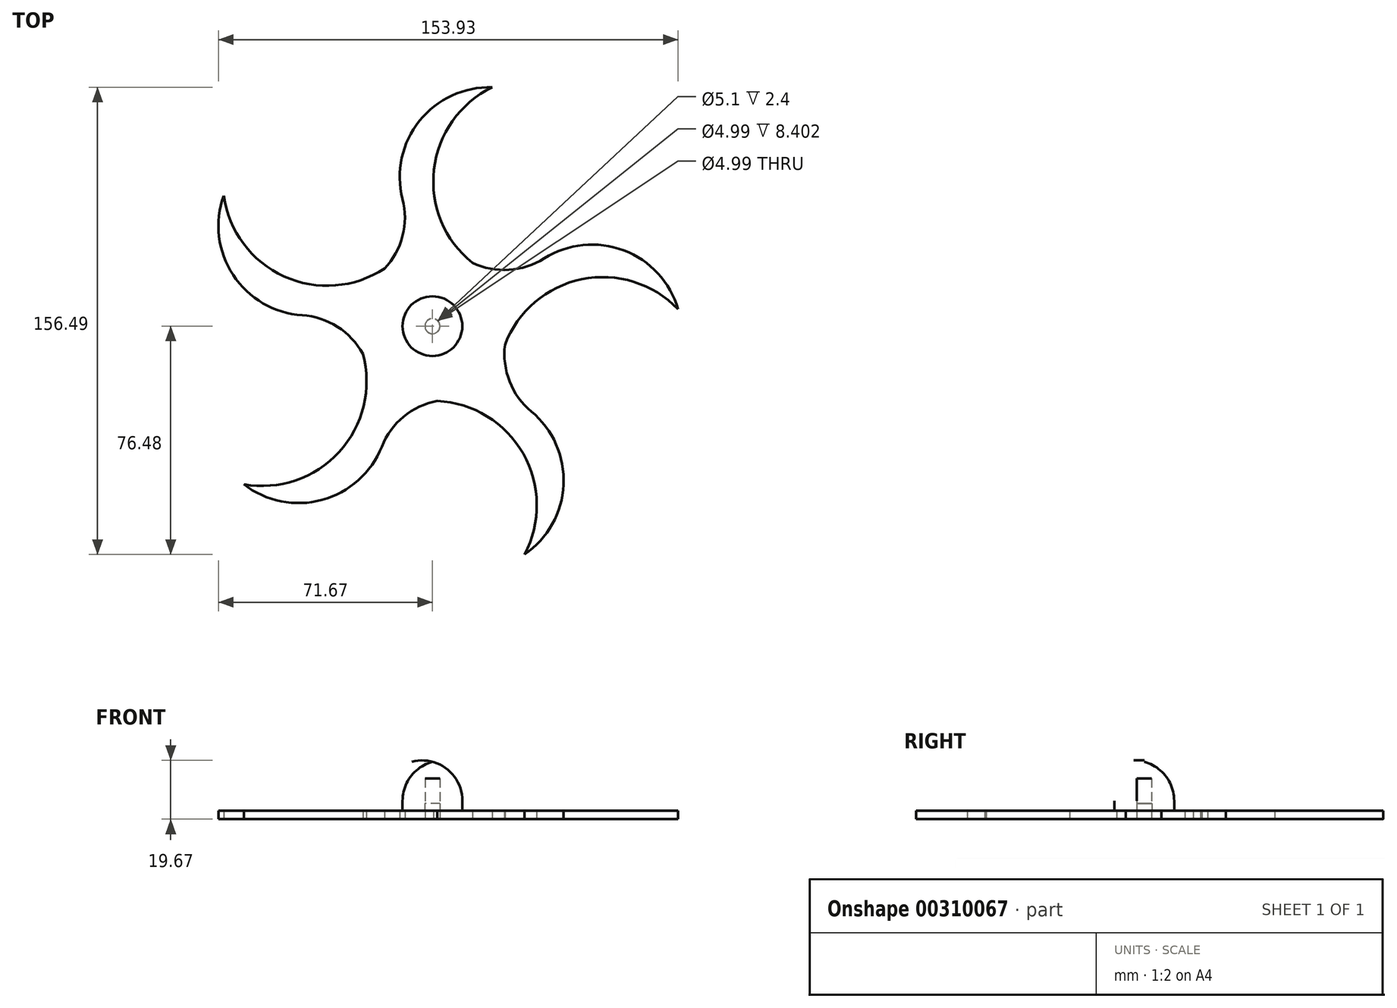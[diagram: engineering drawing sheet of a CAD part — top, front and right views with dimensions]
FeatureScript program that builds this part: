
annotation { "Feature Type Name" : "Feature", "Feature Type Description" : "" }
export const myFeature = defineFeature(function(context is Context, id is Id, definition is map)
    precondition{}
    {
        {
            var Q0;
            Q0=qCreatedBy(makeId("Top.planeOp"),FACE);
            var sketch = newSketch(context, id + "F0", { "sketchPlane" : qUnion([Q0])});
            skCircle(sketch, "E0", {"center": v(0, 0) * mm, "radius": 2.5 * mm});
            skCircle(sketch, "E1", {"center": v(0, 0) * mm, "radius": 25 * mm});
            skArc(sketch, "E2", {"start": v(20, 80) * mm, "mid": v(0.43, 51.6) * mm, "end": v(14.7, 20.22) * mm});
            skArc(sketch, "E3", {"start": v(20, 80) * mm, "mid": v(-9.56, 58.97) * mm, "end": v(2.74, 24.85) * mm});
            skArc(sketch, "E4", {"start": v(-17.11, 18.22) * mm, "mid": v(-10.23, 29.45) * mm, "end": v(-10, 42.61) * mm});
            skArc(sketch, "E5.1.0", {"start": v(-22.62, -10.64) * mm, "mid": v(-31.17, -0.63) * mm, "end": v(-43.62, 3.66) * mm});
            skArc(sketch, "E5.1.1", {"start": v(-69.9, 43.74) * mm, "mid": v(-59.04, 9.13) * mm, "end": v(-22.79, 10.29) * mm});
            skArc(sketch, "E5.1.2", {"start": v(-69.9, 43.74) * mm, "mid": v(-48.95, 16.36) * mm, "end": v(-14.68, 20.23) * mm});
            skArc(sketch, "E5.2.0", {"start": v(3.13, -24.8) * mm, "mid": v(-9.04, -29.84) * mm, "end": v(-16.96, -40.35) * mm});
            skArc(sketch, "E5.2.1", {"start": v(-63.2, -52.97) * mm, "mid": v(-26.93, -53.33) * mm, "end": v(-16.82, -18.5) * mm});
            skArc(sketch, "E5.2.2", {"start": v(-63.2, -52.97) * mm, "mid": v(-30.68, -41.5) * mm, "end": v(-23.78, -7.71) * mm});
            skArc(sketch, "E6.4.3.0", {"start": v(30.84, -76.48) * mm, "mid": v(42.4, -42.1) * mm, "end": v(12.39, -21.71) * mm});
            skArc(sketch, "E6.7.3.0", {"start": v(24.56, -4.68) * mm, "mid": v(25.58, -17.81) * mm, "end": v(33.14, -28.6) * mm});
            skArc(sketch, "E6.8.3.0", {"start": v(30.84, -76.48) * mm, "mid": v(29.98, -42) * mm, "end": v(-0.02, -25) * mm});
            skArc(sketch, "E7.4.4.0", {"start": v(82.26, 5.7) * mm, "mid": v(53.13, 27.31) * mm, "end": v(24.48, 5.07) * mm});
            skArc(sketch, "E7.7.4.0", {"start": v(12.04, 21.9) * mm, "mid": v(24.85, 18.83) * mm, "end": v(37.44, 22.68) * mm});
            skArc(sketch, "E7.8.4.0", {"start": v(82.26, 5.7) * mm, "mid": v(49.21, 15.54) * mm, "end": v(23.77, -7.74) * mm});
            skSolve(sketch);
        }
        {
            var Q0;
            {var subQ4=sQuery(id+"F0.wireOp",EDGE,"E1");var subQ6=sQuery(id+"F0.wireOp",EDGE,"E4");var subQ7=makeQuery(id+"F0.imprint","INTERSECT",VERTEX,{"derivedFrom":[subQ4,subQ6]});Q0=makeQuery(id+"F0.imprint","IMPRINT",FACE,{"disambiguationData":[TD([[makeQuery(id+"F0.imprint","IMPRINT",EDGE,{"disambiguationData":[TD([[subQ7,-1.0]])],"derivedFrom":subQ4}),-1.0]])]});}
            var Q1;
            {var subQ0=sQuery(id+"F0.wireOp",EDGE,"E5.1.1");var subQ1=sQuery(id+"F0.wireOp",EDGE,"E1");var subQ2=makeQuery(id+"F0.imprint","INTERSECT",VERTEX,{"derivedFrom":[subQ1,subQ0]});Q1=makeQuery(id+"F0.imprint","IMPRINT",FACE,{"disambiguationData":[TD([[makeQuery(id+"F0.imprint","IMPRINT",EDGE,{"disambiguationData":[TD([[subQ2,-1.0]])],"derivedFrom":subQ1}),-1.0]])]});}
            var Q2;
            {var subQ0=sQuery(id+"F0.wireOp",EDGE,"E3");var subQ1=sQuery(id+"F0.wireOp",EDGE,"E1");var subQ2=makeQuery(id+"F0.imprint","INTERSECT",VERTEX,{"derivedFrom":[subQ1,subQ0]});Q2=makeQuery(id+"F0.imprint","IMPRINT",FACE,{"disambiguationData":[TD([[makeQuery(id+"F0.imprint","IMPRINT",EDGE,{"disambiguationData":[TD([[subQ2,-1.0]])],"derivedFrom":subQ1}),-1.0]])]});}
            var Q3;
            {var subQ0=sQuery(id+"F0.wireOp",EDGE,"E4");var subQ1=sQuery(id+"F0.wireOp",EDGE,"E1");var subQ2=makeQuery(id+"F0.imprint","INTERSECT",VERTEX,{"derivedFrom":[subQ1,subQ0]});Q3=makeQuery(id+"F0.imprint","IMPRINT",FACE,{"disambiguationData":[TD([[makeQuery(id+"F0.imprint","IMPRINT",EDGE,{"disambiguationData":[TD([[subQ2,1.0]])],"derivedFrom":subQ1}),-1.0]])]});}
            var Q4;
            Q4=makeQuery(id+"F0.imprint","IMPRINT",FACE,{"disambiguationData":[TD([[makeQuery(id+"F0.imprint","IMPRINT",EDGE,{"derivedFrom":sQuery(id+"F0.wireOp",EDGE,"E0")}),-1.0]])]});
            var Q5;
            {var subQ0=sQuery(id+"F0.wireOp",EDGE,"E3");var subQ1=sQuery(id+"F0.wireOp",EDGE,"E1");var subQ2=makeQuery(id+"F0.imprint","INTERSECT",VERTEX,{"derivedFrom":[subQ1,subQ0]});Q5=makeQuery(id+"F0.imprint","IMPRINT",FACE,{"disambiguationData":[TD([[makeQuery(id+"F0.imprint","IMPRINT",EDGE,{"disambiguationData":[TD([[subQ2,1.0]])],"derivedFrom":subQ1}),-1.0]])]});}
            var Q6;
            {var subQ0=sQuery(id+"F0.wireOp",EDGE,"E2");var subQ1=sQuery(id+"F0.wireOp",EDGE,"E1");var subQ2=makeQuery(id+"F0.imprint","INTERSECT",VERTEX,{"derivedFrom":[subQ1,subQ0]});Q6=makeQuery(id+"F0.imprint","IMPRINT",FACE,{"disambiguationData":[TD([[makeQuery(id+"F0.imprint","IMPRINT",EDGE,{"disambiguationData":[TD([[subQ2,1.0]])],"derivedFrom":subQ1}),-1.0]])]});}
            var Q7;
            {var subQ1=sQuery(id+"F0.wireOp",EDGE,"E1");var subQ4=sQuery(id+"F0.wireOp",EDGE,"E6.7.3.0");var subQ5=makeQuery(id+"F0.imprint","INTERSECT",VERTEX,{"derivedFrom":[subQ1,subQ4]});Q7=makeQuery(id+"F0.imprint","IMPRINT",FACE,{"disambiguationData":[TD([[makeQuery(id+"F0.imprint","IMPRINT",EDGE,{"disambiguationData":[TD([[subQ5,-1.0]])],"derivedFrom":subQ1}),-1.0]])]});}
            var Q8;
            {var subQ0=sQuery(id+"F0.wireOp",EDGE,"E6.4.3.0");var subQ1=sQuery(id+"F0.wireOp",EDGE,"E1");var subQ2=makeQuery(id+"F0.imprint","INTERSECT",VERTEX,{"derivedFrom":[subQ1,subQ0]});Q8=makeQuery(id+"F0.imprint","IMPRINT",FACE,{"disambiguationData":[TD([[makeQuery(id+"F0.imprint","IMPRINT",EDGE,{"disambiguationData":[TD([[subQ2,-1.0]])],"derivedFrom":subQ1}),-1.0]])]});}
            var Q9;
            {var subQ1=sQuery(id+"F0.wireOp",EDGE,"E1");var subQ6=sQuery(id+"F0.wireOp",EDGE,"E5.2.0");var subQ7=makeQuery(id+"F0.imprint","INTERSECT",VERTEX,{"derivedFrom":[subQ1,subQ6]});Q9=makeQuery(id+"F0.imprint","IMPRINT",FACE,{"disambiguationData":[TD([[makeQuery(id+"F0.imprint","IMPRINT",EDGE,{"disambiguationData":[TD([[subQ7,-1.0]])],"derivedFrom":subQ1}),-1.0]])]});}
            var Q10;
            {var subQ0=sQuery(id+"F0.wireOp",EDGE,"E5.2.1");var subQ1=sQuery(id+"F0.wireOp",EDGE,"E1");var subQ2=makeQuery(id+"F0.imprint","INTERSECT",VERTEX,{"derivedFrom":[subQ1,subQ0]});Q10=makeQuery(id+"F0.imprint","IMPRINT",FACE,{"disambiguationData":[TD([[makeQuery(id+"F0.imprint","IMPRINT",EDGE,{"disambiguationData":[TD([[subQ2,-1.0]])],"derivedFrom":subQ1}),-1.0]])]});}
            var Q11;
            {var subQ2=sQuery(id+"F0.wireOp",EDGE,"E1");var subQ4=sQuery(id+"F0.wireOp",EDGE,"E5.1.0");var subQ5=makeQuery(id+"F0.imprint","INTERSECT",VERTEX,{"derivedFrom":[subQ2,subQ4]});Q11=makeQuery(id+"F0.imprint","IMPRINT",FACE,{"disambiguationData":[TD([[makeQuery(id+"F0.imprint","IMPRINT",EDGE,{"disambiguationData":[TD([[subQ5,-1.0]])],"derivedFrom":subQ2}),-1.0]])]});}
            var Q12;
            {var subQ0=sQuery(id+"F0.wireOp",EDGE,"E5.1.0");var subQ1=sQuery(id+"F0.wireOp",EDGE,"E1");var subQ2=makeQuery(id+"F0.imprint","INTERSECT",VERTEX,{"derivedFrom":[subQ1,subQ0]});Q12=makeQuery(id+"F0.imprint","IMPRINT",FACE,{"disambiguationData":[TD([[makeQuery(id+"F0.imprint","IMPRINT",EDGE,{"disambiguationData":[TD([[subQ2,1.0]])],"derivedFrom":subQ1}),-1.0]])]});}
            var Q13;
            {var subQ0=sQuery(id+"F0.wireOp",EDGE,"E5.2.0");var subQ1=sQuery(id+"F0.wireOp",EDGE,"E1");var subQ2=makeQuery(id+"F0.imprint","INTERSECT",VERTEX,{"derivedFrom":[subQ1,subQ0]});Q13=makeQuery(id+"F0.imprint","IMPRINT",FACE,{"disambiguationData":[TD([[makeQuery(id+"F0.imprint","IMPRINT",EDGE,{"disambiguationData":[TD([[subQ2,1.0]])],"derivedFrom":subQ1}),-1.0]])]});}
            var Q14;
            {var subQ0=sQuery(id+"F0.wireOp",EDGE,"E6.7.3.0");var subQ1=sQuery(id+"F0.wireOp",EDGE,"E1");var subQ2=makeQuery(id+"F0.imprint","INTERSECT",VERTEX,{"derivedFrom":[subQ1,subQ0]});Q14=makeQuery(id+"F0.imprint","IMPRINT",FACE,{"disambiguationData":[TD([[makeQuery(id+"F0.imprint","IMPRINT",EDGE,{"disambiguationData":[TD([[subQ2,1.0]])],"derivedFrom":subQ1}),-1.0]])]});}
            var Q15;
            {var subQ0=sQuery(id+"F0.wireOp",EDGE,"E2");var subQ1=sQuery(id+"F0.wireOp",EDGE,"E1");var subQ2=makeQuery(id+"F0.imprint","INTERSECT",VERTEX,{"derivedFrom":[subQ1,subQ0]});Q15=makeQuery(id+"F0.imprint","IMPRINT",FACE,{"disambiguationData":[TD([[makeQuery(id+"F0.imprint","IMPRINT",EDGE,{"disambiguationData":[TD([[subQ2,-1.0]])],"derivedFrom":subQ1}),-1.0]])]});}
            extrude(context, id + "F1", {"entities" : qUnion([Q0, Q1, Q2, Q3, Q4, Q5, Q6, Q7, Q8, Q9, Q10, Q11, Q12, Q13, Q14, Q15]), "depth" : 2.8 * mm});
        }
        {
            var Q0;
            Q0=makeQuery(id+"F1.opExtrude","CAP_FACE",FACE,{"disambiguationData":[OSD([sQuery(id+"F0.wireOp",EDGE,"E0"),sQuery(id+"F0.wireOp",EDGE,"E2"),sQuery(id+"F0.wireOp",EDGE,"E3"),sQuery(id+"F0.wireOp",EDGE,"E4"),sQuery(id+"F0.wireOp",EDGE,"E5.1.0"),sQuery(id+"F0.wireOp",EDGE,"E5.1.1"),sQuery(id+"F0.wireOp",EDGE,"E5.1.2"),sQuery(id+"F0.wireOp",EDGE,"E5.2.0"),sQuery(id+"F0.wireOp",EDGE,"E5.2.1"),sQuery(id+"F0.wireOp",EDGE,"E5.2.2"),sQuery(id+"F0.wireOp",EDGE,"E6.4.3.0"),sQuery(id+"F0.wireOp",EDGE,"E6.7.3.0"),sQuery(id+"F0.wireOp",EDGE,"E6.8.3.0"),sQuery(id+"F0.wireOp",EDGE,"E7.4.4.0"),sQuery(id+"F0.wireOp",EDGE,"E7.7.4.0"),sQuery(id+"F0.wireOp",EDGE,"E7.8.4.0")])],"isStart":false});
            var sketch = newSketch(context, id + "F2", { "sketchPlane" : qUnion([Q0])});
            skCircle(sketch, "E8.0", {"center": v(0, 0) * mm, "radius": 2.5 * mm});
            skCircle(sketch, "E9", {"center": v(0, 0) * mm, "radius": 10 * mm});
            skLineSegment(sketch, "E10", {"start": v(-10, 0) * mm, "end": v(-2.5, 0) * mm});
            skLineSegment(sketch, "E11", {"start": v(-2.5, 0) * mm, "end": v(2.5, 0) * mm});
            skLineSegment(sketch, "E12", {"start": v(2.5, 0) * mm, "end": v(10, 0) * mm});
            skCircle(sketch, "E13", {"center": v(0, 0) * mm, "radius": 2.55 * mm});
            skSolve(sketch);
        }
        {
            var Q0;
            {var subQ0=sQuery(id+"F2.wireOp",EDGE,"E10");var subQ1=sQuery(id+"F2.wireOp",EDGE,"E9");var subQ2=makeQuery(id+"F2.imprint","INTERSECT",VERTEX,{"derivedFrom":[subQ1,subQ0]});Q0=makeQuery(id+"F2.imprint","IMPRINT",FACE,{"disambiguationData":[TD([[makeQuery(id+"F2.imprint","IMPRINT",EDGE,{"disambiguationData":[TD([[subQ2,-1.0]])],"derivedFrom":subQ1}),1.0]])]});}
            var Q1;
            {var subQ0=sQuery(id+"F2.wireOp",EDGE,"E10");var subQ1=sQuery(id+"F2.wireOp",EDGE,"E9");var subQ2=makeQuery(id+"F2.imprint","INTERSECT",VERTEX,{"derivedFrom":[subQ1,subQ0]});Q1=makeQuery(id+"F2.imprint","IMPRINT",FACE,{"disambiguationData":[TD([[makeQuery(id+"F2.imprint","IMPRINT",EDGE,{"disambiguationData":[TD([[subQ2,1.0]])],"derivedFrom":subQ1}),1.0]])]});}
            extrude(context, id + "F3", {"entities" : qUnion([Q0, Q1]), "depth" : 2.4 * mm});
        }
        {
            var Q0;
            Q0=makeQuery(id+"F3.opExtrude","CAP_FACE",FACE,{"disambiguationData":[OSD([sQuery(id+"F2.wireOp",EDGE,"E8.0"),sQuery(id+"F2.wireOp",EDGE,"E9")])],"isStart":false});
            var sketch = newSketch(context, id + "F4", { "sketchPlane" : qUnion([Q0])});
            skLineSegment(sketch, "E14.0", {"start": v(-10, 0) * mm, "end": v(-2.5, 0) * mm});
            skLineSegment(sketch, "E15.0", {"start": v(2.5, 0) * mm, "end": v(10, 0) * mm});
            skCircle(sketch, "E16.0", {"center": v(0, 0) * mm, "radius": 10 * mm});
            skCircle(sketch, "E17.0", {"center": v(0, 0) * mm, "radius": 2.5 * mm});
            skSolve(sketch);
        }
        {
            var Q0;
            {var subQ0=sQuery(id+"F4.wireOp",EDGE,"E14.0");Q0=makeQuery(id+"F4.imprint","IMPRINT",FACE,{"disambiguationData":[TD([[makeQuery(id+"F4.imprint","IMPRINT",EDGE,{"derivedFrom":subQ0}),1.0]])]});}
            extrude(context, id + "F5", {"entities" : qUnion([Q0]), "depth" : 1 * mm});
        }
        {
            var Q0;
            Q0=makeQuery(id+"F5.opExtrude","SWEPT_FACE",FACE,{"disambiguationData":[OSD([sQuery(id+"F4.wireOp",EDGE,"E14.0")])]});
            var sketch = newSketch(context, id + "F6", { "sketchPlane" : qUnion([Q0])});
            skLineSegment(sketch, "E18.0", {"start": v(-10, 5.2) * mm, "end": v(10, 5.2) * mm});
            skLineSegment(sketch, "E19.0", {"start": v(-10, 6.2) * mm, "end": v(-10, 5.2) * mm});
            skLineSegment(sketch, "E20.0", {"start": v(10, 6.2) * mm, "end": v(10, 5.2) * mm});
            skLineSegment(sketch, "E21.0", {"start": v(-2.5, 6.2) * mm, "end": v(-2.5, 5.2) * mm});
            skLineSegment(sketch, "E22.0", {"start": v(2.5, 6.2) * mm, "end": v(2.5, 5.2) * mm});
            skLineSegment(sketch, "E23.0.0", {"start": v(2.5, 5.2) * mm, "end": v(10, 5.2) * mm});
            skLineSegment(sketch, "E23.0.1", {"start": v(10, 5.2) * mm, "end": v(10, 6.2) * mm});
            skLineSegment(sketch, "E23.0.2", {"start": v(10, 6.2) * mm, "end": v(2.5, 6.2) * mm});
            skLineSegment(sketch, "E24.0", {"start": v(-10, 6.2) * mm, "end": v(-2.5, 6.2) * mm});
            skLineSegment(sketch, "E25", {"start": v(0, 5.2) * mm, "end": v(0, 19.22) * mm});
            skArc(sketch, "E26", {"start": v(0, 19.22) * mm, "mid": v(-7.21, 14.4) * mm, "end": v(-10, 6.2) * mm});
            skLineSegment(sketch, "E27", {"start": v(-2.5, 6.2) * mm, "end": v(-2.5, 13.6) * mm});
            skLineSegment(sketch, "E28", {"start": v(-2.5, 13.6) * mm, "end": v(0, 13.6) * mm});
            skSolve(sketch);
        }
        {
            var Q0;
            {var subQ0=sQuery(id+"F6.wireOp",EDGE,"E19.0");Q0=makeQuery(id+"F6.imprint","IMPRINT",FACE,{"disambiguationData":[TD([[makeQuery(id+"F6.imprint","IMPRINT",EDGE,{"derivedFrom":subQ0}),1.0]])]});}
            var Q1;
            Q1=makeQuery(id+"F6.imprint","IMPRINT",FACE,{"disambiguationData":[TD([[makeQuery(id+"F6.imprint","IMPRINT",EDGE,{"derivedFrom":sQuery(id+"F6.wireOp",EDGE,"E24.0")}),1.0]])]});
            var Q2;
            Q2=sQuery(id+"F6.wireOp",EDGE,"E25");
            revolve(context, id + "F7", {"operationType" : NewBodyOperationType.ADD, "entities" : qUnion([Q0, Q1]), "axis" : qUnion([Q2]), "revolveType" : RevolveType.FULL});
        }
    });
